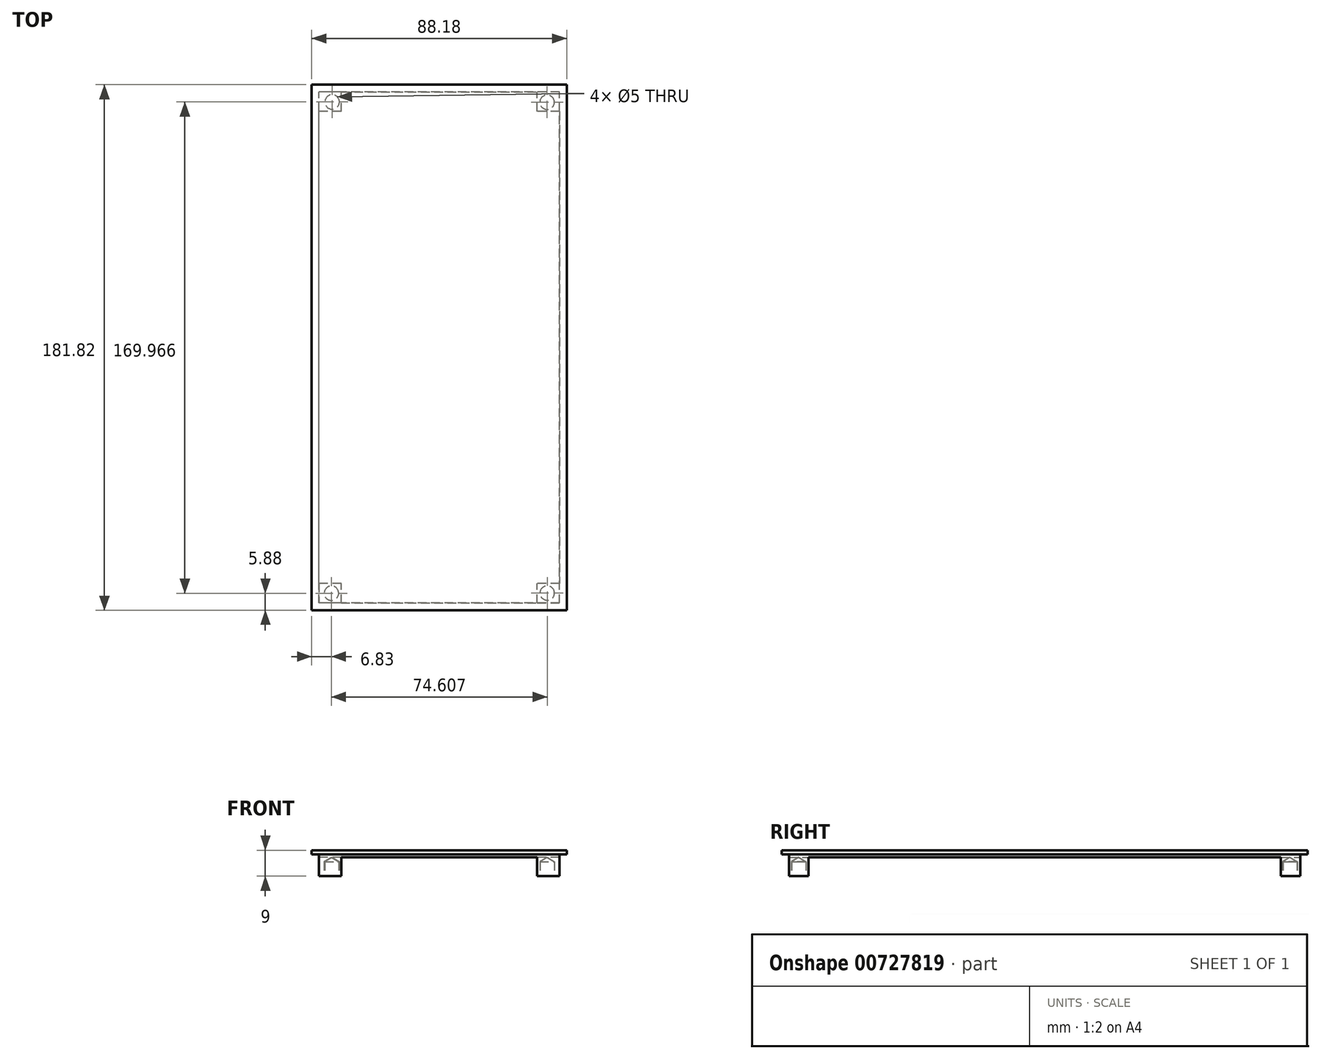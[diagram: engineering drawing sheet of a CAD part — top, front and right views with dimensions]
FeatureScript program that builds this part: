
annotation { "Feature Type Name" : "Feature", "Feature Type Description" : "" }
export const myFeature = defineFeature(function(context is Context, id is Id, definition is map)
    precondition{}
    {
        {
            var Q0;
            Q0=qCreatedBy(makeId("Top.planeOp"),FACE);
            var sketch = newSketch(context, id + "F0", { "sketchPlane" : qUnion([Q0])});
            skLineSegment(sketch, "E0.bottom", {"start": v(44.1, 90.91) * mm, "end": v(-44.1, 90.91) * mm});
            skLineSegment(sketch, "E0.top", {"start": v(44.1, -90.91) * mm, "end": v(-44.1, -90.91) * mm});
            skLineSegment(sketch, "E0.left", {"start": v(44.1, 90.91) * mm, "end": v(44.1, -90.91) * mm});
            skLineSegment(sketch, "E0.right", {"start": v(-44.1, 90.91) * mm, "end": v(-44.1, -90.91) * mm});
            skPoint(sketch, "E0.middle", {"position": v(0, 0) * mm});
            skSolve(sketch);
        }
        {
            var Q0;
            Q0 = qSketchRegion(id + "F0", true);
            var Q1;
            Q1=sQuery(id+"F0.wireOp",EDGE,"E0.top");
            var Q2;
            Q2=sQuery(id+"F0.wireOp",EDGE,"E0.left");
            var Q3;
            Q3=sQuery(id+"F0.wireOp",EDGE,"E0.bottom");
            var Q4;
            Q4=sQuery(id+"F0.wireOp",EDGE,"E0.right");
            extrude(context, id + "F1", {"entities" : qUnion([Q0]), "surfaceEntities" : qUnion([Q1, Q2, Q3, Q4]), "depth" : 2.5 * mm, "offsetDistance" : 25 * mm});
        }
        {
            var Q0;
            Q0=qCreatedBy(makeId("Top.planeOp"),FACE);
            var sketch = newSketch(context, id + "F2", { "sketchPlane" : qUnion([Q0])});
            skLineSegment(sketch, "E1.bottom", {"start": v(44.09, -88.41) * mm, "end": v(-44.1, -88.41) * mm});
            skLineSegment(sketch, "E1.top", {"start": v(44.09, -90.92) * mm, "end": v(-44.1, -90.92) * mm});
            skLineSegment(sketch, "E1.left", {"start": v(44.09, -88.41) * mm, "end": v(44.09, -90.92) * mm});
            skLineSegment(sketch, "E1.right", {"start": v(-44.1, -88.41) * mm, "end": v(-44.1, -90.92) * mm});
            skSolve(sketch);
        }
        {
            var Q0;
            Q0 = qSketchRegion(id + "F2", true);
            extrude(context, id + "F3", {"entities" : qUnion([Q0]), "operationType" : NewBodyOperationType.REMOVE, "depth" : 1 * mm, "offsetDistance" : 25 * mm});
        }
        {
            var Q0;
            Q0=makeQuery(id+"F1.opExtrude","CAP_FACE",FACE,{"disambiguationData":[OSD([sQuery(id+"F0.wireOp",EDGE,"E0.bottom"),sQuery(id+"F0.wireOp",EDGE,"E0.top"),sQuery(id+"F0.wireOp",EDGE,"E0.left"),sQuery(id+"F0.wireOp",EDGE,"E0.right")])],"isStart":true});
            var sketch = newSketch(context, id + "F4", { "sketchPlane" : qUnion([Q0])});
            skLineSegment(sketch, "E2.bottom", {"start": v(44.09, -88.4) * mm, "end": v(-44.1, -88.4) * mm});
            skLineSegment(sketch, "E2.top", {"start": v(44.09, -90.91) * mm, "end": v(-44.1, -90.91) * mm});
            skLineSegment(sketch, "E2.left", {"start": v(44.09, -88.4) * mm, "end": v(44.09, -90.91) * mm});
            skLineSegment(sketch, "E2.right", {"start": v(-44.1, -88.4) * mm, "end": v(-44.1, -90.91) * mm});
            skSolve(sketch);
        }
        {
            var Q0;
            Q0 = qSketchRegion(id + "F4", true);
            extrude(context, id + "F5", {"entities" : qUnion([Q0]), "operationType" : NewBodyOperationType.REMOVE, "oppositeDirection" : true, "depth" : 1 * mm, "offsetDistance" : 25 * mm});
        }
        {
            var Q0;
            Q0=qCreatedBy(makeId("Top.planeOp"),FACE);
            var sketch = newSketch(context, id + "F6", { "sketchPlane" : qUnion([Q0])});
            skLineSegment(sketch, "E3.bottom", {"start": v(44.1, -90.92) * mm, "end": v(41.6, -90.92) * mm});
            skLineSegment(sketch, "E3.top", {"start": v(44.1, 90.91) * mm, "end": v(41.6, 90.91) * mm});
            skLineSegment(sketch, "E3.left", {"start": v(44.1, -90.92) * mm, "end": v(44.1, 90.91) * mm});
            skLineSegment(sketch, "E3.right", {"start": v(41.6, -90.92) * mm, "end": v(41.6, 90.91) * mm});
            skSolve(sketch);
        }
        {
            var Q0;
            Q0 = qSketchRegion(id + "F6", true);
            extrude(context, id + "F7", {"entities" : qUnion([Q0]), "operationType" : NewBodyOperationType.REMOVE, "depth" : 1 * mm, "offsetDistance" : 25 * mm});
        }
        {
            var Q0;
            Q0=qCreatedBy(makeId("Top.planeOp"),FACE);
            var sketch = newSketch(context, id + "F8", { "sketchPlane" : qUnion([Q0])});
            skLineSegment(sketch, "E4.bottom", {"start": v(-41.6, -90.91) * mm, "end": v(-44.1, -90.91) * mm});
            skLineSegment(sketch, "E4.top", {"start": v(-41.6, 90.91) * mm, "end": v(-44.1, 90.91) * mm});
            skLineSegment(sketch, "E4.left", {"start": v(-41.6, -90.91) * mm, "end": v(-41.6, 90.91) * mm});
            skLineSegment(sketch, "E4.right", {"start": v(-44.1, -90.91) * mm, "end": v(-44.1, 90.91) * mm});
            skSolve(sketch);
        }
        {
            var Q0;
            Q0 = qSketchRegion(id + "F8", true);
            extrude(context, id + "F9", {"entities" : qUnion([Q0]), "operationType" : NewBodyOperationType.REMOVE, "depth" : 1 * mm, "offsetDistance" : 25 * mm});
        }
        {
            var Q0;
            Q0=makeQuery(id+"F1.opExtrude","CAP_FACE",FACE,{"disambiguationData":[OSD([sQuery(id+"F0.wireOp",EDGE,"E0.bottom"),sQuery(id+"F0.wireOp",EDGE,"E0.top"),sQuery(id+"F0.wireOp",EDGE,"E0.left"),sQuery(id+"F0.wireOp",EDGE,"E0.right")])],"isStart":true});
            var sketch = newSketch(context, id + "F10", { "sketchPlane" : qUnion([Q0])});
            skLineSegment(sketch, "E5.bottom", {"start": v(41.6, -81.64) * mm, "end": v(33.89, -81.64) * mm});
            skLineSegment(sketch, "E5.top", {"start": v(41.6, -88.4) * mm, "end": v(33.89, -88.4) * mm});
            skLineSegment(sketch, "E5.left", {"start": v(41.6, -81.64) * mm, "end": v(41.6, -88.4) * mm});
            skLineSegment(sketch, "E5.right", {"start": v(33.89, -81.64) * mm, "end": v(33.89, -88.4) * mm});
            skLineSegment(sketch, "E6.bottom", {"start": v(-33.9, -81.64) * mm, "end": v(-41.6, -81.64) * mm});
            skLineSegment(sketch, "E6.top", {"start": v(-33.9, -88.4) * mm, "end": v(-41.6, -88.4) * mm});
            skLineSegment(sketch, "E6.left", {"start": v(-33.9, -81.64) * mm, "end": v(-33.9, -88.4) * mm});
            skLineSegment(sketch, "E6.right", {"start": v(-41.6, -81.64) * mm, "end": v(-41.6, -88.4) * mm});
            skLineSegment(sketch, "E7.bottom", {"start": v(-33.9, 88.41) * mm, "end": v(-41.6, 88.41) * mm});
            skLineSegment(sketch, "E7.top", {"start": v(-33.9, 81.65) * mm, "end": v(-41.6, 81.65) * mm});
            skLineSegment(sketch, "E7.left", {"start": v(-33.9, 88.41) * mm, "end": v(-33.9, 81.65) * mm});
            skLineSegment(sketch, "E7.right", {"start": v(-41.6, 88.41) * mm, "end": v(-41.6, 81.65) * mm});
            skLineSegment(sketch, "E8.bottom", {"start": v(41.6, 88.41) * mm, "end": v(33.89, 88.41) * mm});
            skLineSegment(sketch, "E8.top", {"start": v(41.6, 81.65) * mm, "end": v(33.89, 81.65) * mm});
            skLineSegment(sketch, "E8.left", {"start": v(41.6, 88.41) * mm, "end": v(41.6, 81.65) * mm});
            skLineSegment(sketch, "E8.right", {"start": v(33.89, 88.41) * mm, "end": v(33.89, 81.65) * mm});
            skSolve(sketch);
        }
        {
            var Q0;
            Q0 = qSketchRegion(id + "F10", true);
            extrude(context, id + "F11", {"entities" : qUnion([Q0]), "operationType" : NewBodyOperationType.ADD, "depth" : 6.5 * mm, "offsetDistance" : 25 * mm});
        }
        {
            var Q0;
            Q0=makeQuery(id+"F11.opExtrude","CAP_FACE",FACE,{"disambiguationData":[OSD([sQuery(id+"F10.wireOp",EDGE,"E7.bottom"),sQuery(id+"F10.wireOp",EDGE,"E7.top"),sQuery(id+"F10.wireOp",EDGE,"E7.left"),sQuery(id+"F10.wireOp",EDGE,"E7.right")])],"isStart":false});
            var sketch = newSketch(context, id + "F12", { "sketchPlane" : qUnion([Q0])});
            skCircle(sketch, "E9", {"center": v(-37.26, 85.03) * mm, "radius": 2.37 * mm});
            skSolve(sketch);
        }
        {
            var Q0;
            Q0=makeQuery(id+"F11.opExtrude","CAP_FACE",FACE,{"disambiguationData":[OSD([sQuery(id+"F10.wireOp",EDGE,"E8.bottom"),sQuery(id+"F10.wireOp",EDGE,"E8.top"),sQuery(id+"F10.wireOp",EDGE,"E8.left"),sQuery(id+"F10.wireOp",EDGE,"E8.right")])],"isStart":false});
            var sketch = newSketch(context, id + "F13", { "sketchPlane" : qUnion([Q0])});
            skCircle(sketch, "E10", {"center": v(37.35, 84.96) * mm, "radius": 2.37 * mm});
            skSolve(sketch);
        }
        {
            var Q0;
            Q0=makeQuery(id+"F11.opExtrude","CAP_FACE",FACE,{"disambiguationData":[OSD([sQuery(id+"F10.wireOp",EDGE,"E5.bottom"),sQuery(id+"F10.wireOp",EDGE,"E5.top"),sQuery(id+"F10.wireOp",EDGE,"E5.left"),sQuery(id+"F10.wireOp",EDGE,"E5.right")])],"isStart":false});
            var sketch = newSketch(context, id + "F14", { "sketchPlane" : qUnion([Q0])});
            skCircle(sketch, "E11", {"center": v(37.32, -84.85) * mm, "radius": 2.37 * mm});
            skSolve(sketch);
        }
        {
            var Q0;
            Q0=makeQuery(id+"F11.opExtrude","CAP_FACE",FACE,{"disambiguationData":[OSD([sQuery(id+"F10.wireOp",EDGE,"E6.bottom"),sQuery(id+"F10.wireOp",EDGE,"E6.top"),sQuery(id+"F10.wireOp",EDGE,"E6.left"),sQuery(id+"F10.wireOp",EDGE,"E6.right")])],"isStart":false});
            var sketch = newSketch(context, id + "F15", { "sketchPlane" : qUnion([Q0])});
            skCircle(sketch, "E12", {"center": v(-37.02, -84.94) * mm, "radius": 2.37 * mm});
            skSolve(sketch);
        }
        {
            var Q0;
            Q0=sQuery(id+"F15.wireOp",VERTEX,"E12.center");
            var Q1;
            Q1=sQuery(id+"F14.wireOp",VERTEX,"E11.center");
            var Q2;
            Q2=sQuery(id+"F13.wireOp",VERTEX,"E10.center");
            var Q3;
            Q3=sQuery(id+"F12.wireOp",VERTEX,"E9.center");
            var Q4;
            Q4=makeQuery(id+"F1.opExtrude","SWEPT_BODY",BODY,{"disambiguationData":[OSD([sQuery(id+"F0.wireOp",EDGE,"E0.bottom"),sQuery(id+"F0.wireOp",EDGE,"E0.top"),sQuery(id+"F0.wireOp",EDGE,"E0.left"),sQuery(id+"F0.wireOp",EDGE,"E0.right")])]});
            hole(context, id + "F16", {"style" : HoleStyle.SIMPLE, "endStyle" : HoleEndStyle.BLIND, "holeDiameter" : 5 * mm, "majorDiameter" : 5 * mm, "holeDepth" : 5 * mm, "isTappedThrough" : true, "tappedDepth" : 12 * mm, "tapClearance" : 3, "locations" : qUnion([Q0, Q1, Q2, Q3]), "scope" : qUnion([Q4])});
        }
    });
